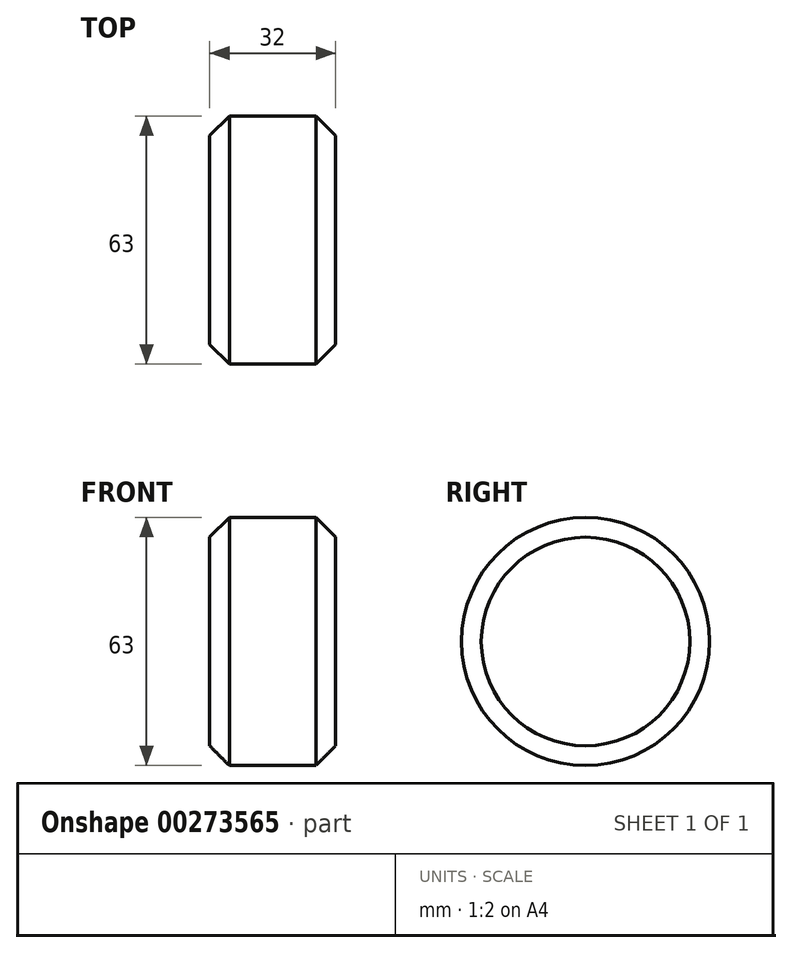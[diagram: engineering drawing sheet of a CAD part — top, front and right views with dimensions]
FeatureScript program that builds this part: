
annotation { "Feature Type Name" : "Feature", "Feature Type Description" : "" }
export const myFeature = defineFeature(function(context is Context, id is Id, definition is map)
    precondition{}
    {
        {
            var Q0;
            Q0=qCreatedBy(makeId("Right.planeOp"),FACE);
            var sketch = newSketch(context, id + "F0", { "sketchPlane" : qUnion([Q0])});
            skCircle(sketch, "E0", {"center": v(0, 0) * mm, "radius": 31.5 * mm});
            skSolve(sketch);
        }
        {
            var Q0;
            Q0 = qSketchRegion(id + "F0", true);
            extrude(context, id + "F1", {"entities" : qUnion([Q0]), "depth" : 32 * mm});
        }
        {
            var Q0;
            Q0=makeQuery(id+"F1.opExtrude","CAP_EDGE",EDGE,{"disambiguationData":[OSD([sQuery(id+"F0.wireOp",EDGE,"E0")])],"isStart":true});
            var Q1;
            Q1=makeQuery(id+"F1.opExtrude","CAP_EDGE",EDGE,{"disambiguationData":[OSD([sQuery(id+"F0.wireOp",EDGE,"E0")])],"isStart":false});
            chamfer(context, id + "F2", {"entities" : qUnion([Q0, Q1]), "width" : 5 * mm, "tangentPropagation" : true});
        }
    });
